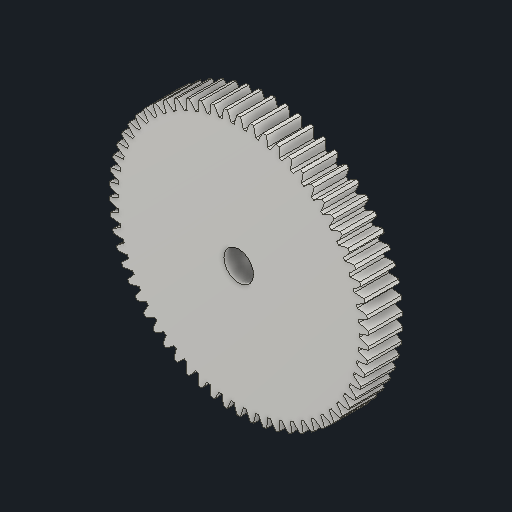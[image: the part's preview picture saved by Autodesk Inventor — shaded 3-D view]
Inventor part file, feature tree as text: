
AUTODESK INVENTOR PART (.ipt)
format: ipt  version: 2025.3 (Build 293356030, 356C)  size: 475,648 bytes
history: native  units: mm (DEFAULTED — no unit token found)
features: plane x3, other x3, extrude x2, sketch x2
ambient origin geometry x8: Origin, YZ Plane, XZ Plane, XY Plane, X Axis, Y Axis, Z Axis, Center Point
bodies: Solid1 (feature_tree)
feature tree (10):
  extrude  "Extrusion1"  Depth=8.0mm TaperAngle=0.0deg
  plane  "Work Plane2"
  plane  "Work Plane8"
  plane  "Work Plane9"
  other  "Spur Gear"
  extrude  "Extrusion2"  Depth=10.0mm TaperAngle=0.0deg
  sketch  "Sketch1"  dims[d0=60.05mm d1=8.0mm d2=0.0mm]
  other  "Srf1"
  sketch  "Sketch3"  dims[d3=58.9mm d4=10.0mm d5=0.0mm d16=40.0mm d17=0.0mm d34=0.506708mm d39=0.0mm d41=0.0mm d43=40.0mm d46=40.0mm d47=0.0mm d48=0.0mm d49=6.85mm d50=0.0mm d51=0.0mm d52=0.5mm d53=0.872665mm d54=0.5mm d55=0.872665mm]
  other  "Pitch Diameter"
